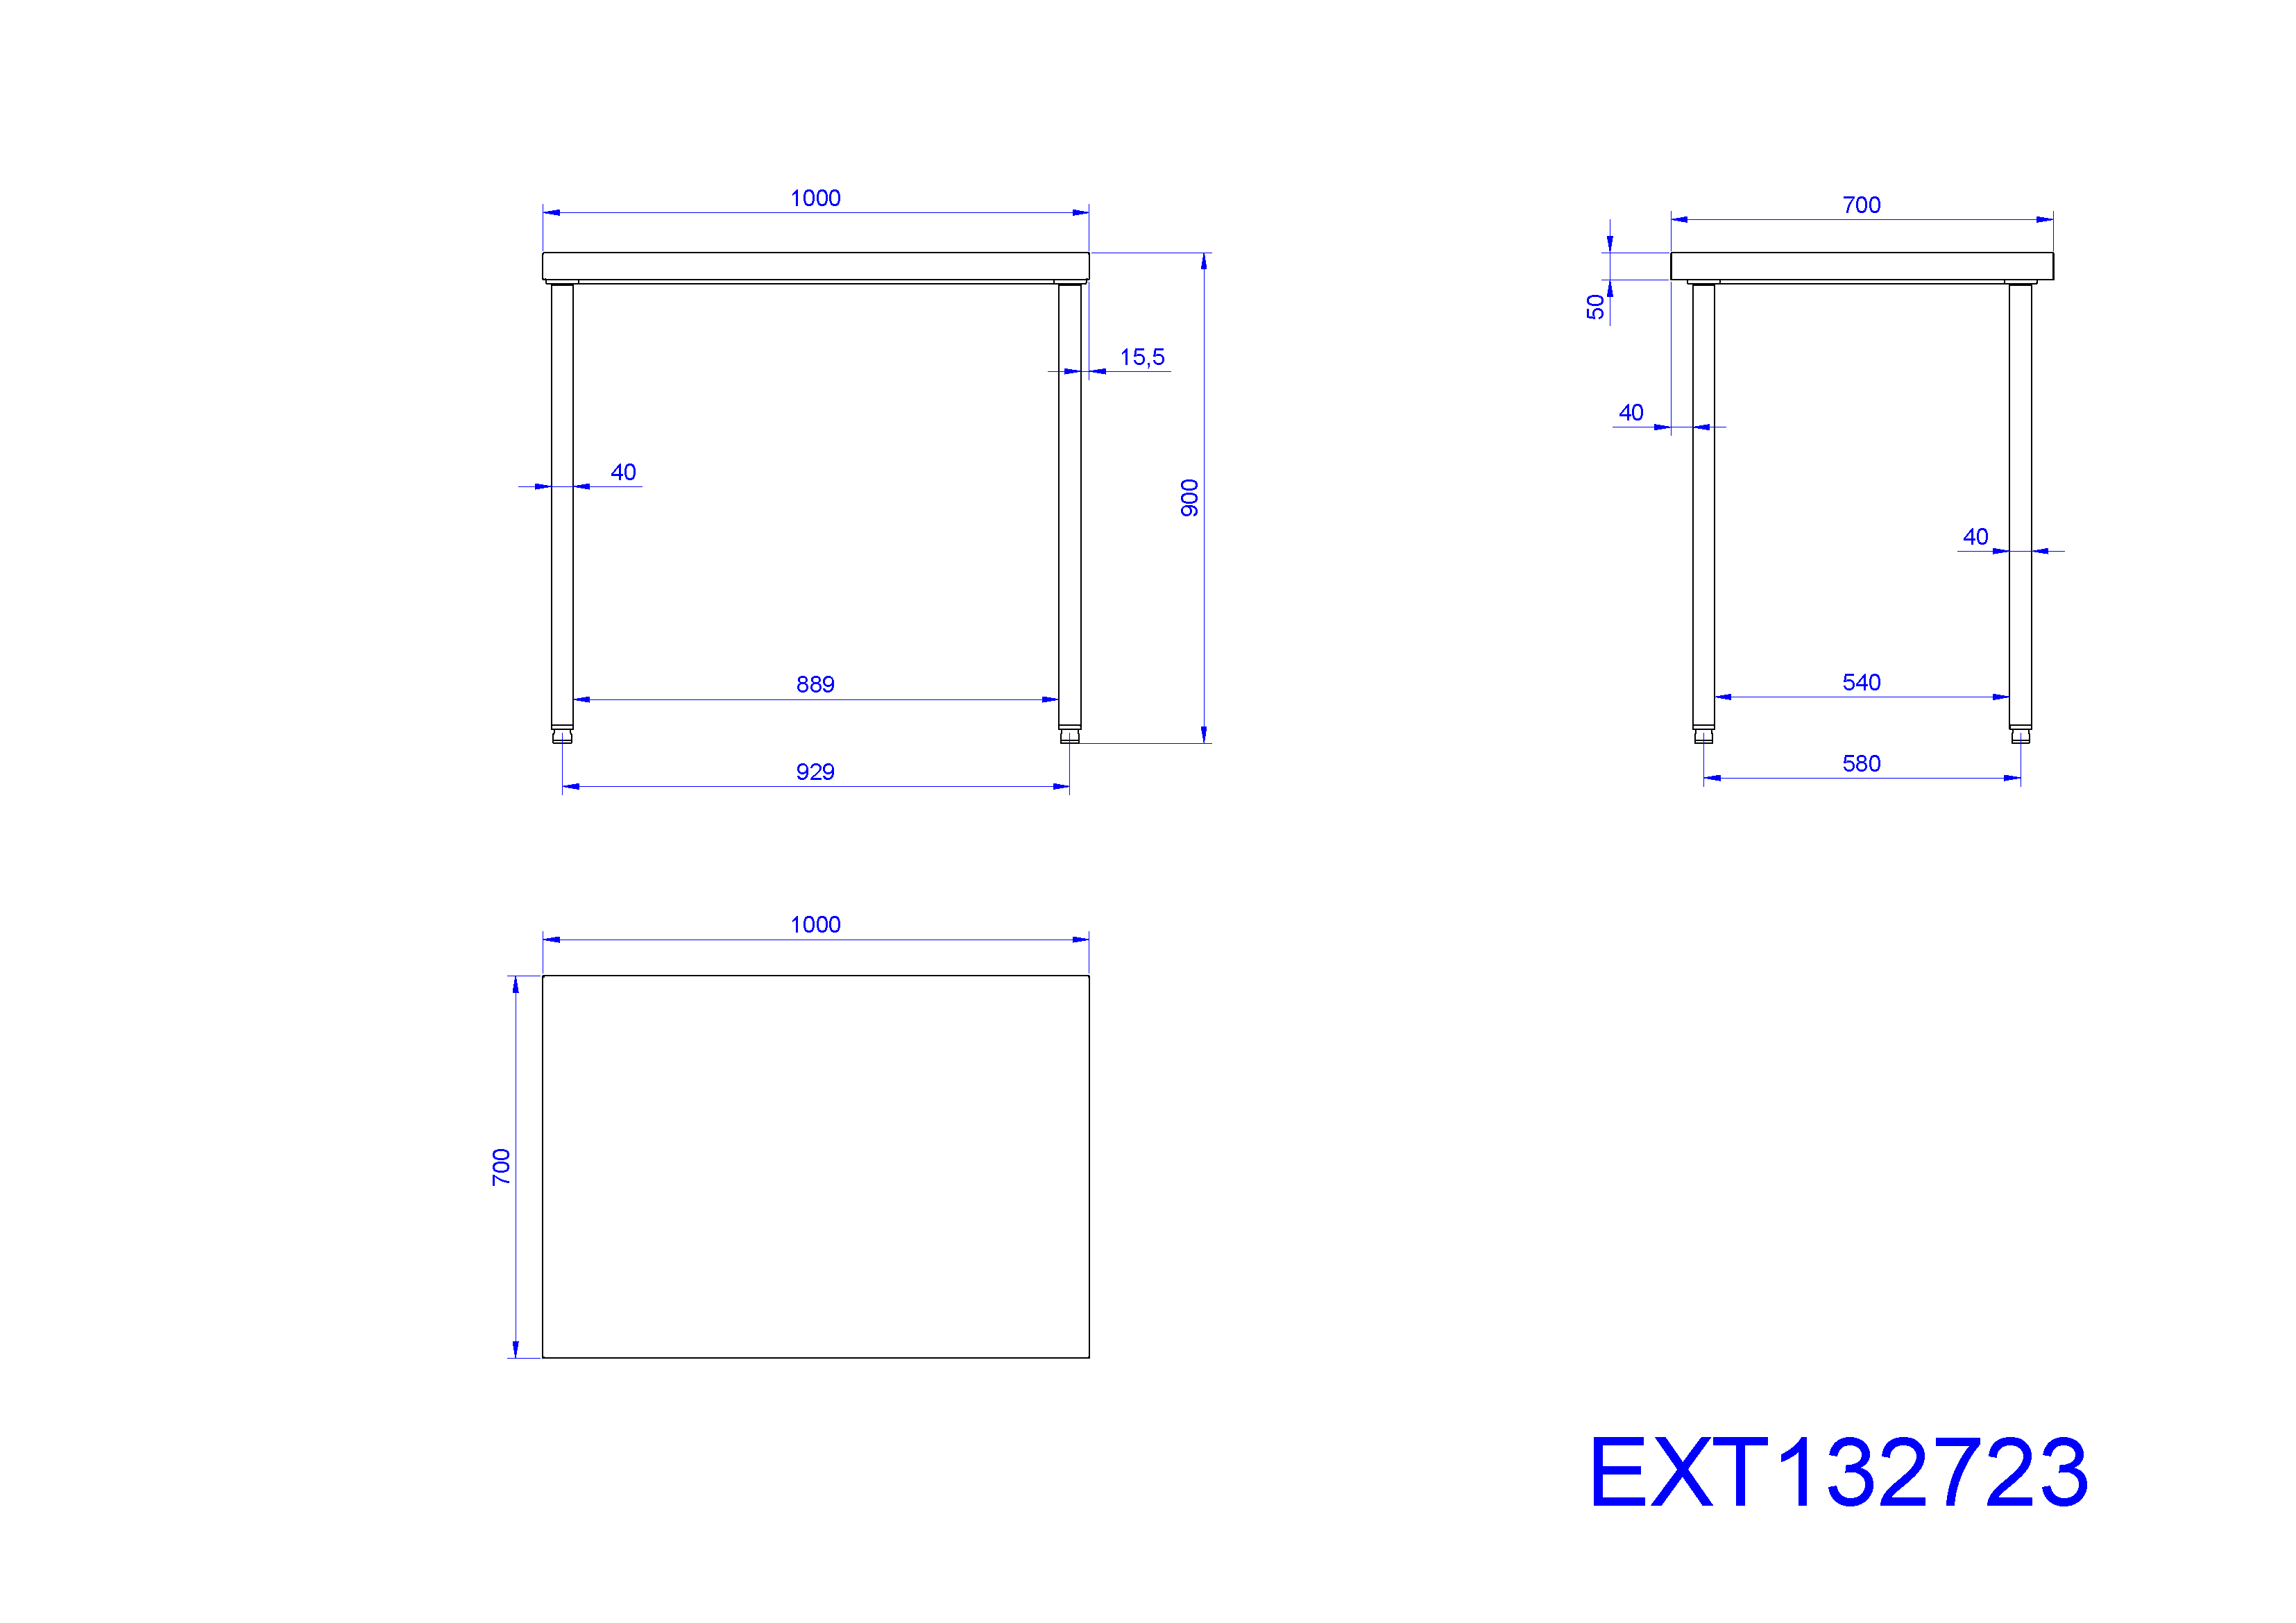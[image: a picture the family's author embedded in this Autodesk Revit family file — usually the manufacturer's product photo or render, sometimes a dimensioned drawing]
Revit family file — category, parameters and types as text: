
# Revit family: QF_ZANUSSI_132841_WTD1407N
name_source: partatom
category: Attrezzature speciali
units: mm (PartAtom-declared; Revit-internal decimal feet)

## family parameters
Basato su piano di lavoro = No
Condiviso = No
Punto di calcolo locali = No
Quota connettore circolare = Usa diametro
Sempre verticale = Sì
Taglio con vuoti quando caricato = No
Tipo di parte = Normale

## types (1)
- Standard
    Accessory = Sì
    Cold Water Size = 0 mm
    Compressed Air Pressure = 0.0 Pa
    Compressed Air Size = 0 mm
    Compressed Air Volume = 0.0 L/s
    Condensate Return Size = 0 mm
    Cycle = 0 Hz
    Depth Actual = 700 mm  [stored 2.29659 ft]
    Descrizione = WORK TABLE-DISASSEMBLED 1400MM
    Direct Waste Size = 0 mm
    Gas Input Pressure = 0
    Gas KW = 0
    Gas Size = 0 mm
    HP = 0 HP
    Height Actual = 900 mm  [stored 2.95276 ft]
    Hot Water Size = 0 mm
    Item Number = 132841
    Length Actual = 1400 mm  [stored 4.59318 ft]
    Modello = WTD1407N
    Phase = 0
    Produttore = Zanussi
    Prospetto di default = 0 mm  [stored 0 ft]
    Refrigerant Compressor Remote = Sì
    Refrigeration Liquid Line Size = 0 mm  [stored 0 ft]
    Refrigeration Suction Line Size = 0 mm  [stored 0 ft]
    Steam Consumption per Hour = 0
    Steam Supply Maximum Pressure = 0.0 Pa
    Steam Supply Minimum Pressure = 0.0 Pa
    Steam Supply Size = 0 mm
    URL = http://www.zanussiprofessional.com
    URL Manufacturer = http://www.zanussiprofessional.com
    Volts = 0 V
    Watts = 0 W
    Weight = 47.00 kg

note: source unit labels omitted for Gas Input Pressure — the stored unit's dimension contradicts the parameter name (converter mislabeling)

note: [stored X ft] marks values corroborated as IEEE doubles in the binary element streams (Revit-internal decimal feet)

## geometry (parser evidence)
native form markers: Sweep x2
no freeform markers — native parametric forms only
